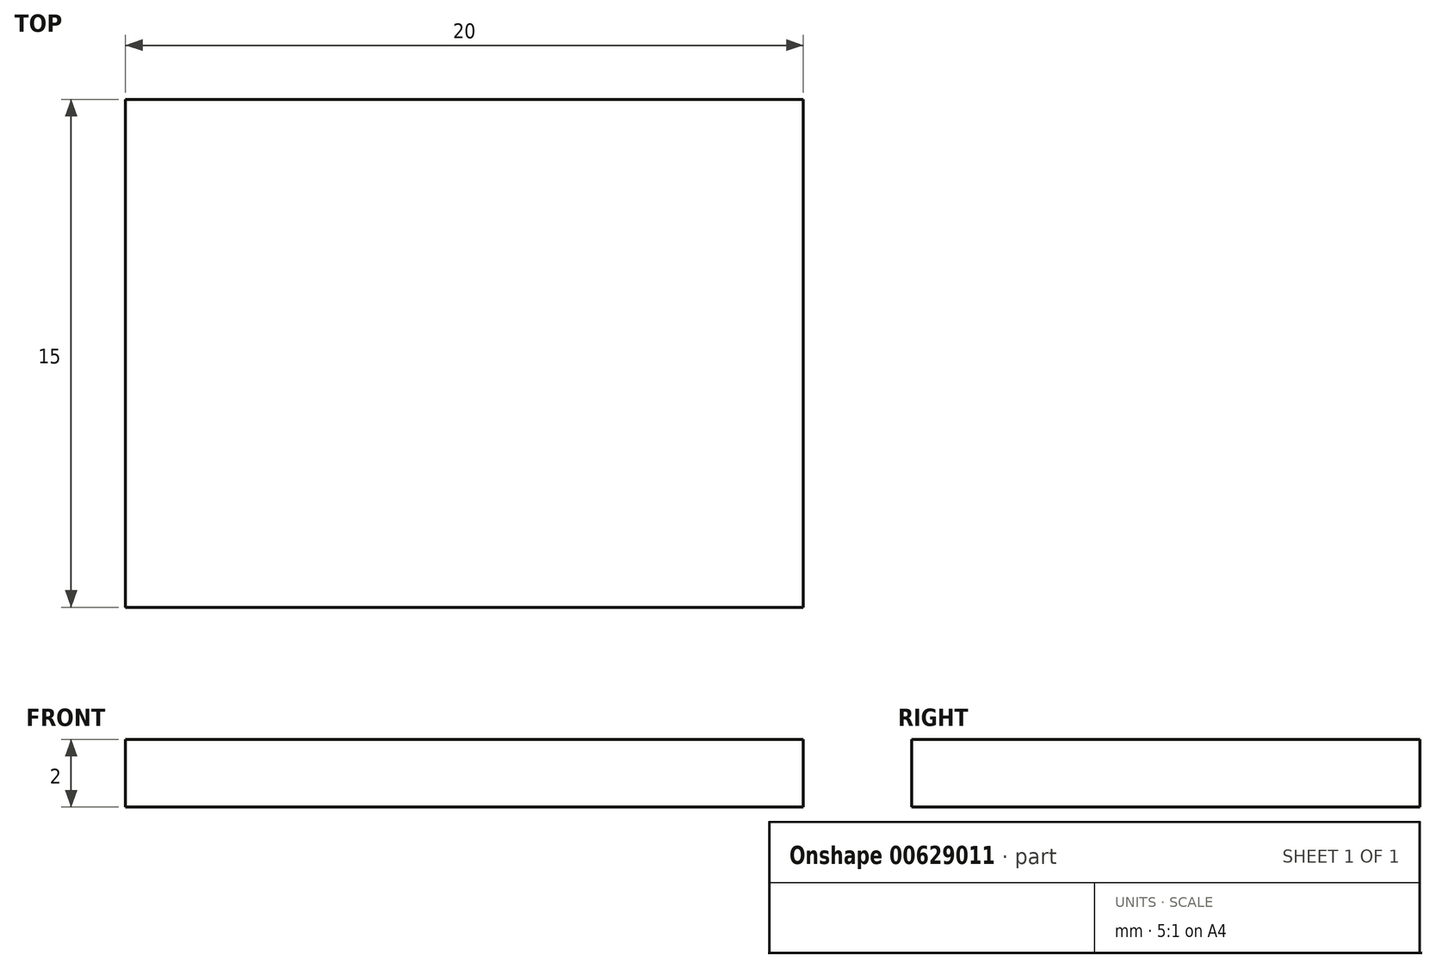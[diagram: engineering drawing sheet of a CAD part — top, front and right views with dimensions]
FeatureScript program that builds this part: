
annotation { "Feature Type Name" : "Feature", "Feature Type Description" : "" }
export const myFeature = defineFeature(function(context is Context, id is Id, definition is map)
    precondition{}
    {
        {
            var Q0;
            Q0=qCreatedBy(makeId("Top.planeOp"),FACE);
            var sketch = newSketch(context, id + "F0", { "sketchPlane" : qUnion([Q0])});
            skLineSegment(sketch, "E0.bottom", {"start": v(-6.35, 12.42) * mm, "end": v(13.65, 12.42) * mm});
            skLineSegment(sketch, "E0.top", {"start": v(-6.35, -2.58) * mm, "end": v(13.65, -2.58) * mm});
            skLineSegment(sketch, "E0.left", {"start": v(-6.35, 12.42) * mm, "end": v(-6.35, -2.58) * mm});
            skLineSegment(sketch, "E0.right", {"start": v(13.65, 12.42) * mm, "end": v(13.65, -2.58) * mm});
            skSolve(sketch);
        }
        {
            var Q0;
            Q0=makeQuery(id+"F0.imprint","IMPRINT",FACE,{"disambiguationData":[TD([[makeQuery(id+"F0.imprint","IMPRINT",EDGE,{"derivedFrom":sQuery(id+"F0.wireOp",EDGE,"E0.bottom")}),-1.0]])]});
            extrude(context, id + "F1", {"entities" : qUnion([Q0]), "depth" : 2 * mm, "offsetDistance" : 25 * mm});
        }
    });
